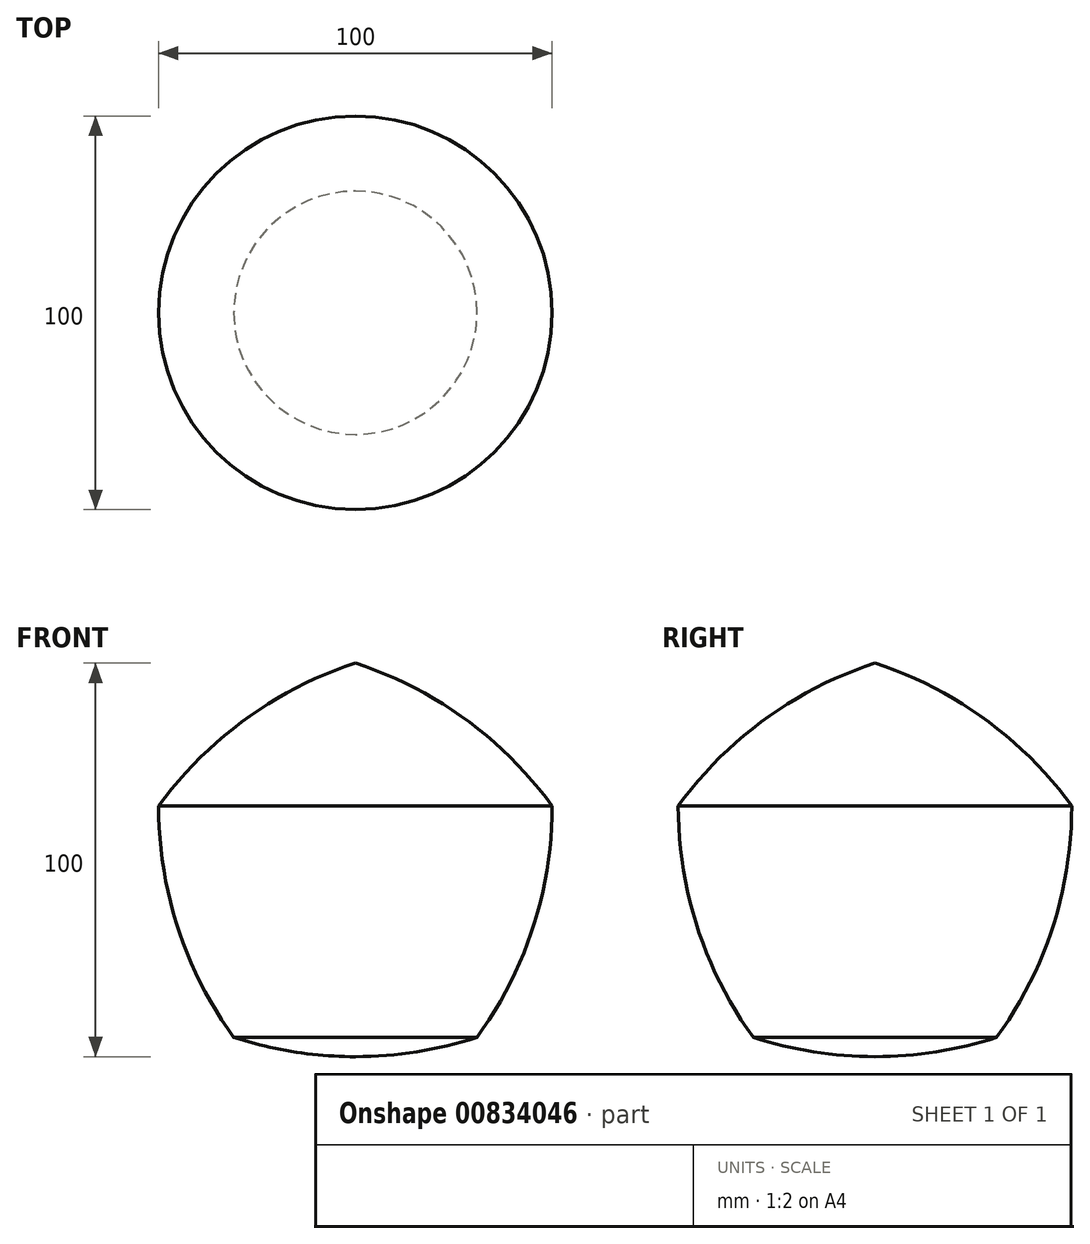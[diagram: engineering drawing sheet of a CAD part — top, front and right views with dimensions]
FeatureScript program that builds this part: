
annotation { "Feature Type Name" : "Feature", "Feature Type Description" : "" }
export const myFeature = defineFeature(function(context is Context, id is Id, definition is map)
    precondition{}
    {
        {
            var Q0;
            Q0=qCreatedBy(makeId("Front.planeOp"),FACE);
            var sketch = newSketch(context, id + "F0", { "sketchPlane" : qUnion([Q0])});
            skCircle(sketch, "E0.cCircle", {"center": v(0, 0) * mm, "radius": 42.53 * mm, "construction": true});
            skLineSegment(sketch, "E0.0", {"start": v(0, 52.57) * mm, "end": v(50, 16.25) * mm, "construction": true});
            skLineSegment(sketch, "E0.1", {"start": v(50, 16.25) * mm, "end": v(30.9, -42.53) * mm, "construction": true});
            skLineSegment(sketch, "E0.2", {"start": v(30.9, -42.53) * mm, "end": v(-30.9, -42.53) * mm, "construction": true});
            skLineSegment(sketch, "E0.3", {"start": v(-30.9, -42.53) * mm, "end": v(-50, 16.25) * mm, "construction": true});
            skLineSegment(sketch, "E0.4", {"start": v(-50, 16.25) * mm, "end": v(0, 52.57) * mm, "construction": true});
            skPoint(sketch, "E0.0.midPoint", {"position": v(25, 34.4) * mm});
            skArc(sketch, "E1", {"start": v(-50, 16.25) * mm, "mid": v(-45.1, -14.66) * mm, "end": v(-30.9, -42.53) * mm});
            skArc(sketch, "E2", {"start": v(0, 52.57) * mm, "mid": v(-27.88, 38.37) * mm, "end": v(-50, 16.25) * mm});
            skArc(sketch, "E3", {"start": v(50, 16.25) * mm, "mid": v(27.88, 38.37) * mm, "end": v(0, 52.57) * mm});
            skArc(sketch, "E4", {"start": v(30.9, -42.53) * mm, "mid": v(45.1, -14.66) * mm, "end": v(50, 16.25) * mm});
            skArc(sketch, "E5", {"start": v(-30.9, -42.53) * mm, "mid": v(0, -47.43) * mm, "end": v(30.9, -42.53) * mm});
            skLineSegment(sketch, "E6", {"start": v(0, 52.57) * mm, "end": v(0, -47.43) * mm});
            skSolve(sketch);
        }
        {
            var Q0;
            {var subQ0=sQuery(id+"F0.wireOp",EDGE,"E1");Q0=makeQuery(id+"F0.imprint","IMPRINT",FACE,{"disambiguationData":[TD([[makeQuery(id+"F0.imprint","IMPRINT",EDGE,{"derivedFrom":subQ0}),1.0]])]});}
            var Q1;
            Q1=sQuery(id+"F0.wireOp",EDGE,"E6");
            revolve(context, id + "F1", {"surfaceOperationType" : NewSurfaceOperationType.NEW, "entities" : qUnion([Q0]), "axis" : qUnion([Q1]), "revolveType" : RevolveType.FULL});
        }
    });
